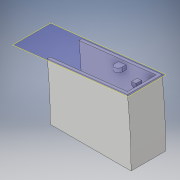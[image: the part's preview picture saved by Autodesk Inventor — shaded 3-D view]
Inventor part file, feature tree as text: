
AUTODESK INVENTOR PART (.ipt)
format: ipt  version: 2017 (Build 210142000, 142)  size: 287,744 bytes
history: native  units: in
note: dims shown in document units (in); Inventor stores cm internally (conversion verified against a paired STEP export)
features: sketch x12, extrude x8, fillet x5, plane x2, sweep x1, shell x1, loft x1, split x1, chamfer x1, other x1
ambient origin geometry x8: Origin, YZ Plane, XZ Plane, XY Plane, X Axis, Y Axis, Z Axis, Center Point
bodies: Solid1 (feature_tree)
feature tree (33):
  sweep  "Sweep1"
  shell  "Shell1"  Thickness=0.0in
  extrude  "Extrusion1"  Depth=0.0591in
  extrude  "Extrusion2"  Depth=0.0787in
  fillet  "Fillet1"  Radius=0.0787in
  plane  "Work Plane1"
  loft  "Loft1"
  fillet  "Fillet2"  Radius=0.0984in
  fillet  "Fillet3"  Radius=0.1969in
  fillet  "Fillet4"  [1 undecoded]
  sketch  "Sketch6"  dims[d26=0.0394in d27=0.0394in]
  extrude  "Extrusion3"  Depth=0.0394in
  extrude  "Extrusion4"  Depth=0.0394in
  extrude  "Extrusion5"  Depth=0.0591in TaperAngle=0.0deg
  fillet  "Fillet5"  Radius=0.0591in
  plane  "Work Plane2"
  split  "Split1"
  extrude  "Extrusion7"  Depth=0.0787in
  extrude  "Extrusion8"  Depth=0.0787in
  chamfer  "Chamfer1"  Distance=0.1575in
  extrude  "Extrusion9"  Depth=0.0945in
  sketch  "Sketch1"  dims[d0=1.6732in d1=0.7087in d4=0.0in d5=0.0in]
  sketch  "Sketch2"  dims[d6=0.0591in d8=0.5118in]
  sketch  "Sketch3"  dims[d9=90.0deg d10=0.0984in d11=0.0787in d12=0.0in]
  sketch  "Sketch4"  dims[d16=0.0394in d17=1.1024in d18=0.0in d19=0.0984in d20=0.1969in d21=0.0in d22=90.0deg]
  sketch  "Sketch5"  dims[d23=0.0in d24=90.0deg d25=0.0394in]
  other  "Edges1"
  sketch  "Sketch7"  dims[d28=0.0591in d29=0.0in d30=0.0591in d31=0.0in d32=0.0591in]
  sketch  "Sketch8"  dims[d33=0.1575in d34=0.0787in]
  sketch  "Sketch9"  dims[d35=0.1575in d36=0.0in d37=0.0787in]
  sketch  "Sketch11"  dims[d41=0.0in]
  sketch  "Sketch12"  dims[d42=0.1181in]
  sketch  "Sketch13"  dims[d43=0.0787in d44=0.1575in d45=0.0in d46=0.0945in d47=0.0591in d48=0.0in d49=0.0787in d50=0.0787in d51=45.0deg d54=0.0197in d55=0.0197in d56=10.6299in d57=1.1811in d58=0.0in]
note: 1 required parameter value undecoded (feature->parameter linkage not recoverable at this tier; creation-order binding heuristic only, values carry confidence <= 0.55)
